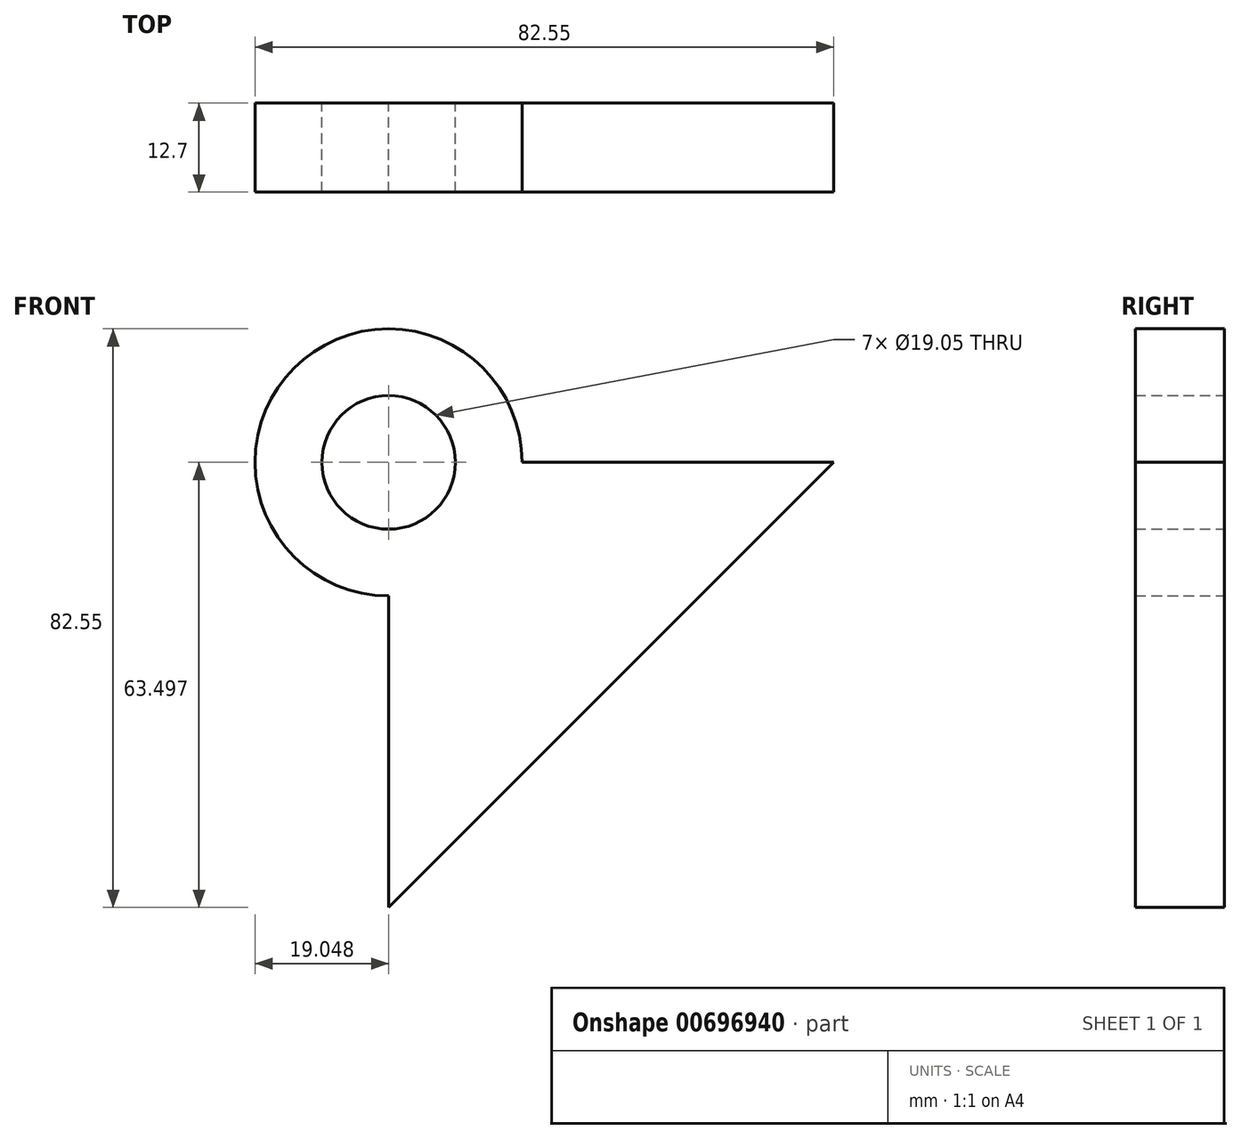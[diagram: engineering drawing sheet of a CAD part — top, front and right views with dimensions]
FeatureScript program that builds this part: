
annotation { "Feature Type Name" : "Feature", "Feature Type Description" : "" }
export const myFeature = defineFeature(function(context is Context, id is Id, definition is map)
    precondition{}
    {
        {
            var Q0;
            Q0=qCreatedBy(makeId("Front.planeOp"),FACE);
            var sketch = newSketch(context, id + "F0", { "sketchPlane" : qUnion([Q0])});
            skLineSegment(sketch, "E0", {"start": v(-45.4, -28.66) * mm, "end": v(18.1, 34.84) * mm});
            skArc(sketch, "E1", {"start": v(-26.34, 34.84) * mm, "mid": v(-58.86, 48.3) * mm, "end": v(-45.4, 15.79) * mm});
            skCircle(sketch, "E2", {"center": v(-45.4, 34.84) * mm, "radius": 9.53 * mm});
            skLineSegment(sketch, "E3.trimOffspring", {"start": v(-26.34, 34.84) * mm, "end": v(18.1, 34.84) * mm});
            skLineSegment(sketch, "E4.trimOffspring", {"start": v(-45.4, 15.79) * mm, "end": v(-45.4, -28.66) * mm});
            skSolve(sketch);
        }
        {
            var Q0;
            Q0=makeQuery(id+"F0.imprint","IMPRINT",FACE,{"disambiguationData":[TD([[makeQuery(id+"F0.imprint","IMPRINT",EDGE,{"derivedFrom":sQuery(id+"F0.wireOp",EDGE,"E0")}),1.0]])]});
            extrude(context, id + "F1", {"entities" : qUnion([Q0]), "depth" : 12.7 * mm, "offsetDistance" : 25.4 * mm});
        }
    });
